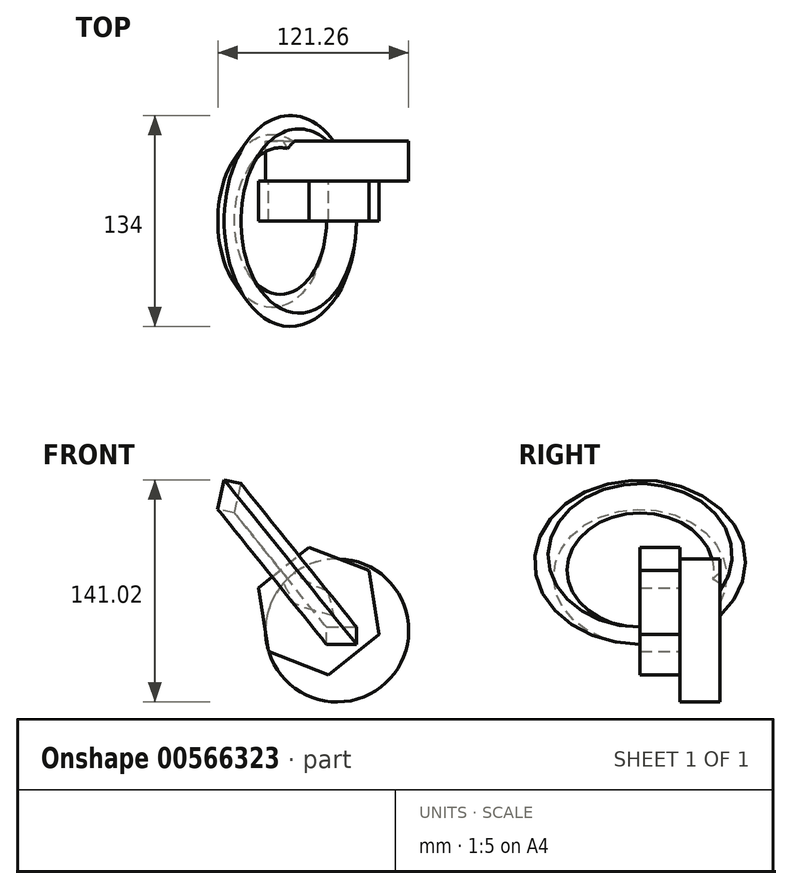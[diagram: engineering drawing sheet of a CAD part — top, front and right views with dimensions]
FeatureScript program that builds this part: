
annotation { "Feature Type Name" : "Feature", "Feature Type Description" : "" }
export const myFeature = defineFeature(function(context is Context, id is Id, definition is map)
    precondition{}
    {
        {
            var Q0;
            Q0=qCreatedBy(makeId("Front.planeOp"),FACE);
            var sketch = newSketch(context, id + "F0", { "sketchPlane" : qUnion([Q0])});
            skCircle(sketch, "E0", {"center": v(-0.33, -2.1) * mm, "radius": 45.45 * mm});
            skPoint(sketch, "E0.first.point", {"position": v(-38.84, 22.04) * mm});
            skPoint(sketch, "E0.second.point", {"position": v(35.55, 25.8) * mm});
            skPoint(sketch, "E0.third.point", {"position": v(31.74, -34.31) * mm});
            skSolve(sketch);
        }
        {
            var Q0;
            Q0=makeQuery(id+"F0.imprint","IMPRINT",FACE,{"disambiguationData":[TD([[makeQuery(id+"F0.imprint","IMPRINT",EDGE,{"derivedFrom":sQuery(id+"F0.wireOp",EDGE,"E0")}),1.0]])]});
            extrude(context, id + "F1", {"entities" : qUnion([Q0]), "depth" : 25.4 * mm, "offsetDistance" : 25.4 * mm});
        }
        {
            var Q0;
            Q0=makeQuery(id+"F1.opExtrude","CAP_FACE",FACE,{"disambiguationData":[OSD([sQuery(id+"F0.wireOp",EDGE,"E0")])],"isStart":false});
            var sketch = newSketch(context, id + "F2", { "sketchPlane" : qUnion([Q0])});
            skCircle(sketch, "E1.cCircle", {"center": v(-12.01, 10.17) * mm, "radius": 35.54 * mm, "construction": true});
            skLineSegment(sketch, "E1.0", {"start": v(19.95, 35.91) * mm, "end": v(26.26, -4.64) * mm});
            skLineSegment(sketch, "E1.1", {"start": v(26.26, -4.64) * mm, "end": v(-5.7, -30.37) * mm});
            skLineSegment(sketch, "E1.2", {"start": v(-5.7, -30.37) * mm, "end": v(-43.97, -15.56) * mm});
            skLineSegment(sketch, "E1.3", {"start": v(-43.97, -15.56) * mm, "end": v(-50.28, 24.99) * mm});
            skLineSegment(sketch, "E1.4", {"start": v(-50.28, 24.99) * mm, "end": v(-18.32, 50.72) * mm});
            skLineSegment(sketch, "E1.5", {"start": v(-18.32, 50.72) * mm, "end": v(19.95, 35.91) * mm});
            skPoint(sketch, "E1.0.midPoint", {"position": v(23.1, 15.64) * mm});
            skSolve(sketch);
        }
        {
            var Q0;
            Q0 = qSketchRegion(id + "F2", true);
            extrude(context, id + "F3", {"entities" : qUnion([Q0]), "operationType" : NewBodyOperationType.ADD, "depth" : 25.4 * mm, "offsetDistance" : 25.4 * mm});
        }
        {
            var Q0;
            Q0=makeQuery(id+"F3.opExtrude","CAP_FACE",FACE,{"disambiguationData":[OSD([sQuery(id+"F2.wireOp",EDGE,"E1.0"),sQuery(id+"F2.wireOp",EDGE,"E1.1"),sQuery(id+"F2.wireOp",EDGE,"E1.2"),sQuery(id+"F2.wireOp",EDGE,"E1.3"),sQuery(id+"F2.wireOp",EDGE,"E1.4"),sQuery(id+"F2.wireOp",EDGE,"E1.5")])],"isStart":false});
            var sketch = newSketch(context, id + "F4", { "sketchPlane" : qUnion([Q0])});
            skLineSegment(sketch, "E2.bottom", {"start": v(11.98, 0) * mm, "end": v(-7.1, 0) * mm});
            skLineSegment(sketch, "E2.top", {"start": v(11.98, -10.9) * mm, "end": v(-7.1, -10.9) * mm});
            skLineSegment(sketch, "E2.left", {"start": v(11.98, 0) * mm, "end": v(11.98, -10.9) * mm});
            skLineSegment(sketch, "E2.right", {"start": v(-7.1, 0) * mm, "end": v(-7.1, -10.9) * mm});
            skSolve(sketch);
        }
        {
            var Q0;
            Q0=makeQuery(id+"F4.imprint","IMPRINT",FACE,{"disambiguationData":[TD([[makeQuery(id+"F4.imprint","IMPRINT",EDGE,{"derivedFrom":sQuery(id+"F4.wireOp",EDGE,"E2.bottom")}),1.0]])]});
            var Q1;
            Q1=makeQuery(id+"F3.opExtrude","CAP_EDGE",EDGE,{"disambiguationData":[OSD([sQuery(id+"F2.wireOp",EDGE,"E1.4")])],"isStart":false});
            revolve(context, id + "F5", {"operationType" : NewBodyOperationType.ADD, "entities" : qUnion([Q0]), "axis" : qUnion([Q1]), "revolveType" : RevolveType.FULL});
        }
    });
